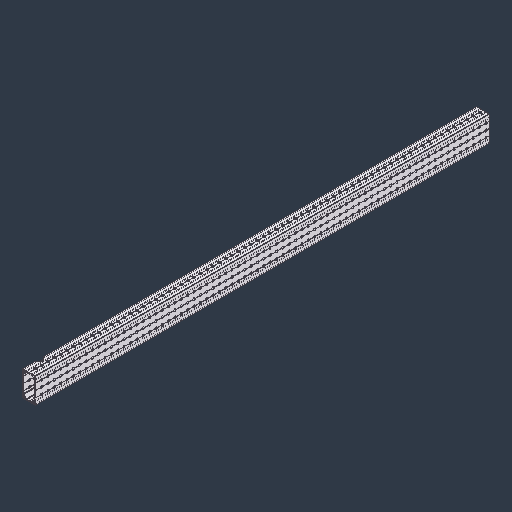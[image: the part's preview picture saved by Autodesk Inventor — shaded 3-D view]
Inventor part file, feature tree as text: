
AUTODESK INVENTOR PART (.ipt)
format: ipt  version: 2024.3 (Build 283343000, 343)  size: 4,487,168 bytes
history: native  units: mm
features: extrude x2, sketch x2, mirror x1, other x1
ambient origin geometry x8: Origin, YZ Plane, XZ Plane, XY Plane, X Axis, Y Axis, Z Axis, Center Point
bodies: Solid1 (feature_tree)
feature tree (6):
  extrude  "Extrusion2"  Depth=19.05mm
  extrude  "Extrusion3"  Depth=6.35mm
  mirror  "Mirror1"
  sketch  "Sketch2"  dims[d4=908.05mm d5=0.0mm d6=19.05mm]
  sketch  "Sketch4"  dims[d7=33.3375mm d8=4.7625mm d9=6.35mm d10=0.0mm]
  other  "LPattern2"
